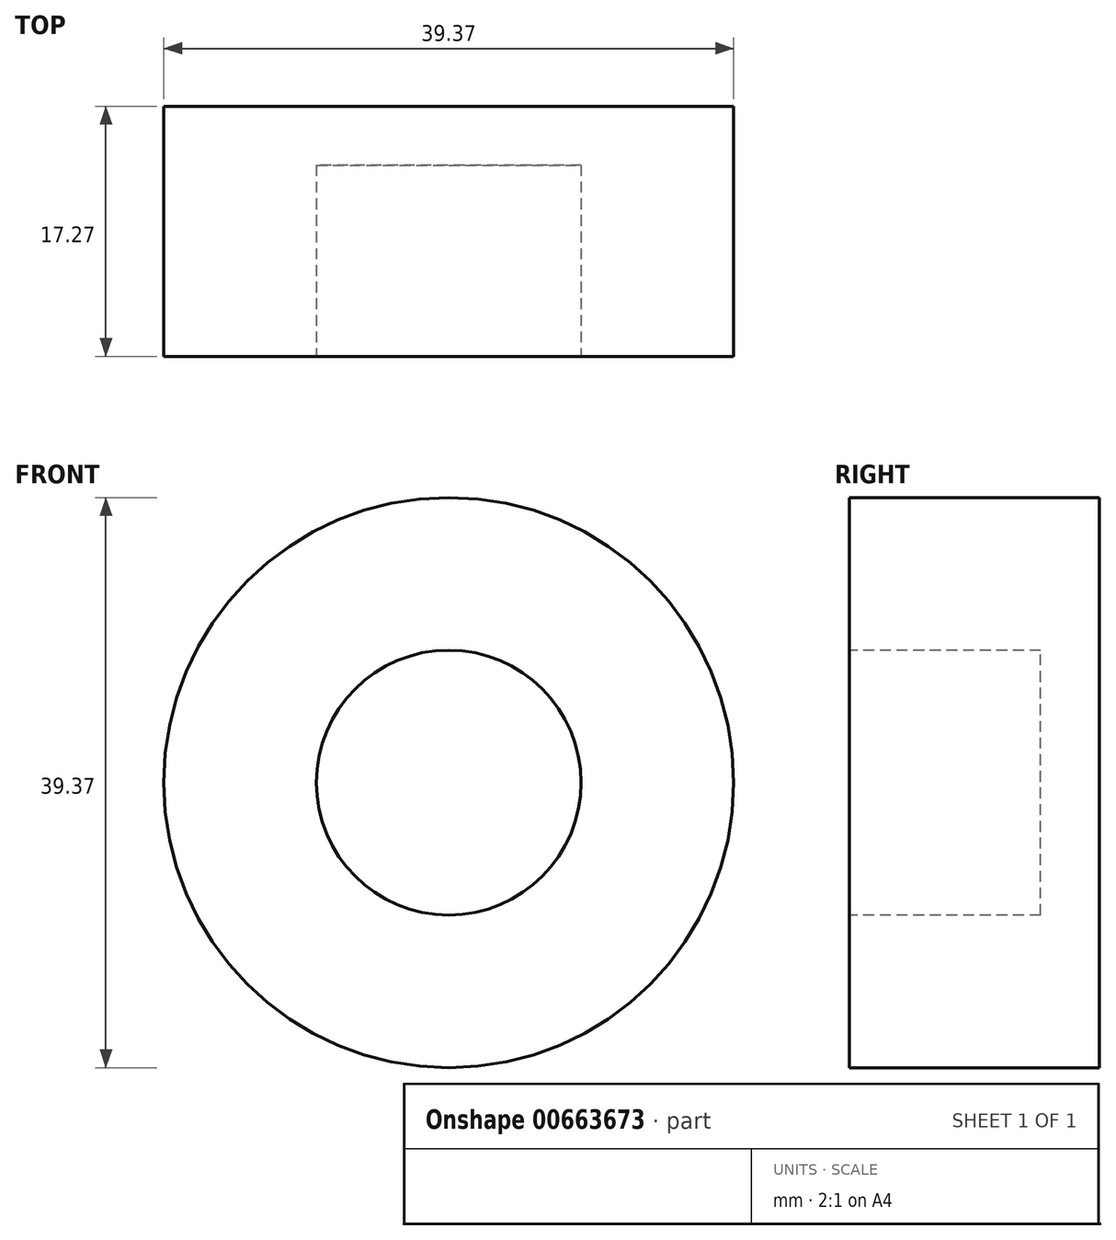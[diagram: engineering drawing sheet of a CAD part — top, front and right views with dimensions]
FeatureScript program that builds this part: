
annotation { "Feature Type Name" : "Feature", "Feature Type Description" : "" }
export const myFeature = defineFeature(function(context is Context, id is Id, definition is map)
    precondition{}
    {
        {
            var Q0;
            Q0=qCreatedBy(makeId("Front.planeOp"),FACE);
            var sketch = newSketch(context, id + "F0", { "sketchPlane" : qUnion([Q0])});
            skCircle(sketch, "E0", {"center": v(251.2, 74.85) * mm, "radius": 19.69 * mm});
            skSolve(sketch);
        }
        {
            var Q0;
            Q0=makeQuery(id+"F0.imprint","IMPRINT",FACE,{"disambiguationData":[TD([[makeQuery(id+"F0.imprint","IMPRINT",EDGE,{"derivedFrom":sQuery(id+"F0.wireOp",EDGE,"E0")}),1.0]])]});
            extrude(context, id + "F1", {"entities" : qUnion([Q0]), "depth" : 17.27 * mm, "offsetDistance" : 25.4 * mm});
        }
        {
            var Q0;
            Q0=makeQuery(id+"F1.opExtrude","CAP_FACE",FACE,{"disambiguationData":[OSD([sQuery(id+"F0.wireOp",EDGE,"E0")])],"isStart":false});
            var sketch = newSketch(context, id + "F2", { "sketchPlane" : qUnion([Q0])});
            skCircle(sketch, "E1.0.0", {"center": v(251.2, 74.85) * mm, "radius": 19.69 * mm});
            skCircle(sketch, "E2", {"center": v(251.2, 74.85) * mm, "radius": 9.14 * mm});
            skSolve(sketch);
        }
        {
            var Q0;
            Q0=makeQuery(id+"F2.imprint","IMPRINT",FACE,{"disambiguationData":[TD([[makeQuery(id+"F2.imprint","IMPRINT",EDGE,{"derivedFrom":sQuery(id+"F2.wireOp",EDGE,"E2")}),1.0]])]});
            extrude(context, id + "F3", {"entities" : qUnion([Q0]), "operationType" : NewBodyOperationType.REMOVE, "oppositeDirection" : true, "depth" : 13.2 * mm, "offsetDistance" : 25.4 * mm});
        }
        {
            var Q0;
            Q0=makeQuery(id+"F3.boolean.opBoolean","COPY",FACE,{"derivedFrom":makeQuery(id+"F3.opExtrude","CAP_FACE",FACE,{"disambiguationData":[OSD([sQuery(id+"F2.wireOp",EDGE,"E2")])],"isStart":false})});
            var sketch = newSketch(context, id + "F4", { "sketchPlane" : qUnion([Q0])});
            skCircle(sketch, "E3", {"center": v(256.55, 78.63) * mm, "radius": 2 * mm});
            skCircle(sketch, "E4.1.0", {"center": v(125.8, 237) * mm, "radius": 2 * mm});
            skCircle(sketch, "E4.2.0", {"center": v(-78.63, 256.55) * mm, "radius": 2 * mm});
            skPoint(sketch, "E4.center", {"position": v(0, 0) * mm});
            skCircle(sketch, "E5.1.3.0", {"center": v(-237, 125.8) * mm, "radius": 2 * mm});
            skCircle(sketch, "E5.1.4.0", {"center": v(-256.55, -78.63) * mm, "radius": 2 * mm});
            skCircle(sketch, "E5.1.5.0", {"center": v(-125.8, -237) * mm, "radius": 2 * mm});
            skCircle(sketch, "E5.1.6.0", {"center": v(78.63, -256.55) * mm, "radius": 2 * mm});
            skCircle(sketch, "E5.1.7.0", {"center": v(237, -125.8) * mm, "radius": 2 * mm});
            skCircle(sketch, "E6", {"center": v(251.8, 81.68) * mm, "radius": 1.78 * mm});
            skCircle(sketch, "E7", {"center": v(246.62, 80.33) * mm, "radius": 1.68 * mm});
            skCircle(sketch, "E8", {"center": v(245.18, 76.66) * mm, "radius": 1.65 * mm});
            skCircle(sketch, "E9", {"center": v(246.97, 71.3) * mm, "radius": 2 * mm});
            skCircle(sketch, "E10", {"center": v(252.52, 70.67) * mm, "radius": 2.44 * mm});
            skCircle(sketch, "E11", {"center": v(257.18, 74.43) * mm, "radius": 1.65 * mm});
            skSolve(sketch);
        }
        {
            var Q0;
            Q0=makeQuery(id+"F4.imprint","IMPRINT",FACE,{"disambiguationData":[TD([[makeQuery(id+"F4.imprint","IMPRINT",EDGE,{"derivedFrom":sQuery(id+"F4.wireOp",EDGE,"E4.1.0")}),1.0]])]});
            var Q1;
            Q1=makeQuery(id+"F4.imprint","IMPRINT",FACE,{"disambiguationData":[TD([[makeQuery(id+"F4.imprint","IMPRINT",EDGE,{"derivedFrom":sQuery(id+"F4.wireOp",EDGE,"E4.2.0")}),1.0]])]});
            var Q2;
            Q2=makeQuery(id+"F4.imprint","IMPRINT",FACE,{"disambiguationData":[TD([[makeQuery(id+"F4.imprint","IMPRINT",EDGE,{"derivedFrom":sQuery(id+"F4.wireOp",EDGE,"E5.1.3.0")}),1.0]])]});
            var Q3;
            Q3=makeQuery(id+"F4.imprint","IMPRINT",FACE,{"disambiguationData":[TD([[makeQuery(id+"F4.imprint","IMPRINT",EDGE,{"derivedFrom":sQuery(id+"F4.wireOp",EDGE,"E5.1.4.0")}),1.0]])]});
            var Q4;
            Q4=makeQuery(id+"F4.imprint","IMPRINT",FACE,{"disambiguationData":[TD([[makeQuery(id+"F4.imprint","IMPRINT",EDGE,{"derivedFrom":sQuery(id+"F4.wireOp",EDGE,"E5.1.5.0")}),1.0]])]});
            var Q5;
            Q5=makeQuery(id+"F4.imprint","IMPRINT",FACE,{"disambiguationData":[TD([[makeQuery(id+"F4.imprint","IMPRINT",EDGE,{"derivedFrom":sQuery(id+"F4.wireOp",EDGE,"E5.1.6.0")}),1.0]])]});
            var Q6;
            Q6=makeQuery(id+"F4.imprint","IMPRINT",FACE,{"disambiguationData":[TD([[makeQuery(id+"F4.imprint","IMPRINT",EDGE,{"derivedFrom":sQuery(id+"F4.wireOp",EDGE,"E5.1.7.0")}),1.0]])]});
            extrude(context, id + "F5", {"entities" : qUnion([Q0, Q1, Q2, Q3, Q4, Q5, Q6]), "operationType" : NewBodyOperationType.REMOVE, "oppositeDirection" : true, "depth" : 25.4 * mm, "offsetDistance" : 25.4 * mm});
        }
    });
